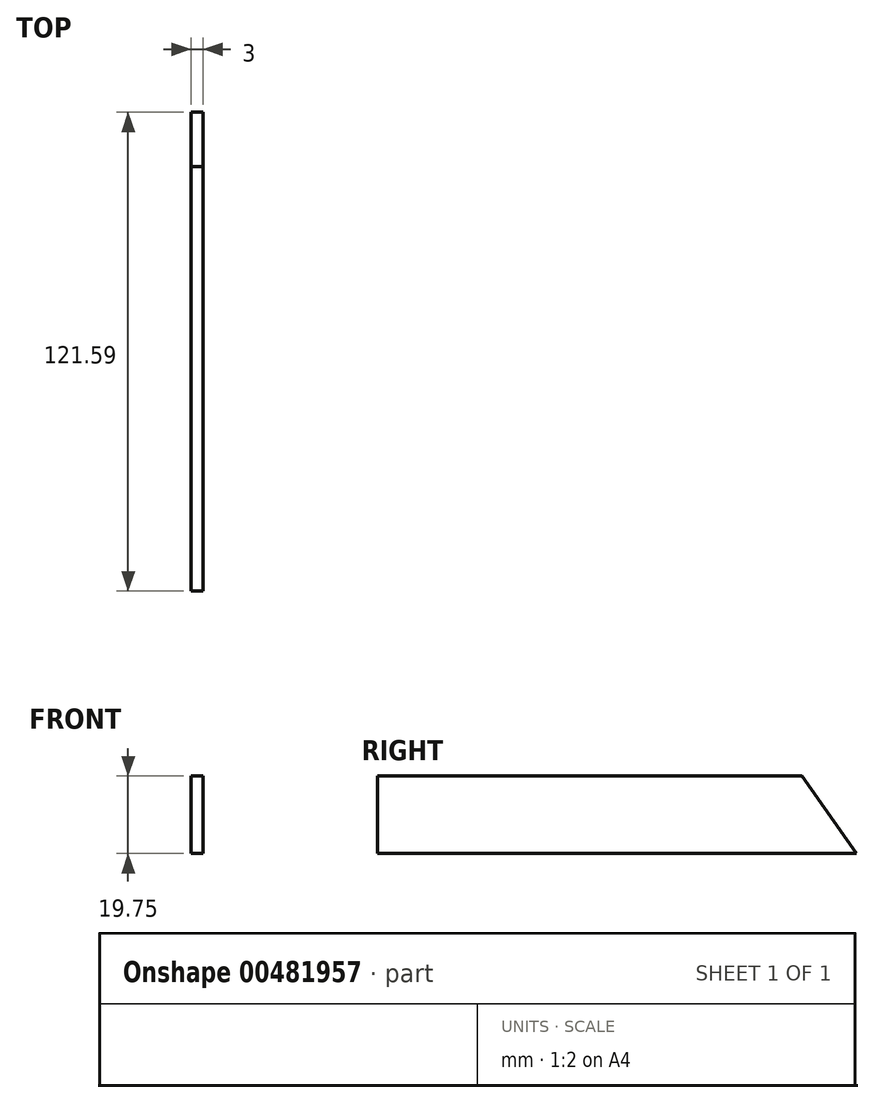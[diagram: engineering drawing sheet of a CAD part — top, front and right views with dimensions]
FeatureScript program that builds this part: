
annotation { "Feature Type Name" : "Feature", "Feature Type Description" : "" }
export const myFeature = defineFeature(function(context is Context, id is Id, definition is map)
    precondition{}
    {
        {
            var Q0;
            Q0=qCreatedBy(makeId("Right.planeOp"),FACE);
            var sketch = newSketch(context, id + "F0", { "sketchPlane" : qUnion([Q0])});
            skLineSegment(sketch, "E0", {"start": v(121.6, 0) * mm, "end": v(0, 0) * mm});
            skLineSegment(sketch, "E1", {"start": v(0, 19.75) * mm, "end": v(107.85, 19.75) * mm});
            skLineSegment(sketch, "E2", {"start": v(107.85, 19.75) * mm, "end": v(121.6, 0) * mm});
            skPoint(sketch, "E3.orphan", {"position": v(0, 50.7) * mm});
            skPoint(sketch, "E4.end.orphan", {"position": v(-0.6, 0) * mm});
            skPoint(sketch, "E4.start.orphan", {"position": v(-4.27, 19.75) * mm});
            skLineSegment(sketch, "E5", {"start": v(0, 0) * mm, "end": v(0, 19.75) * mm});
            skPoint(sketch, "E6.end.orphan", {"position": v(-116.39, 19.75) * mm});
            skPoint(sketch, "E7.orphan", {"position": v(-122.81, 0) * mm});
            skSolve(sketch);
        }
        {
            var Q0;
            Q0=qSketchRegion(id+"F0",true);
            extrude(context, id + "F1", {"entities" : qUnion([Q0]), "depth" : 3 * mm, "offsetDistance" : 25 * mm});
        }
    });
